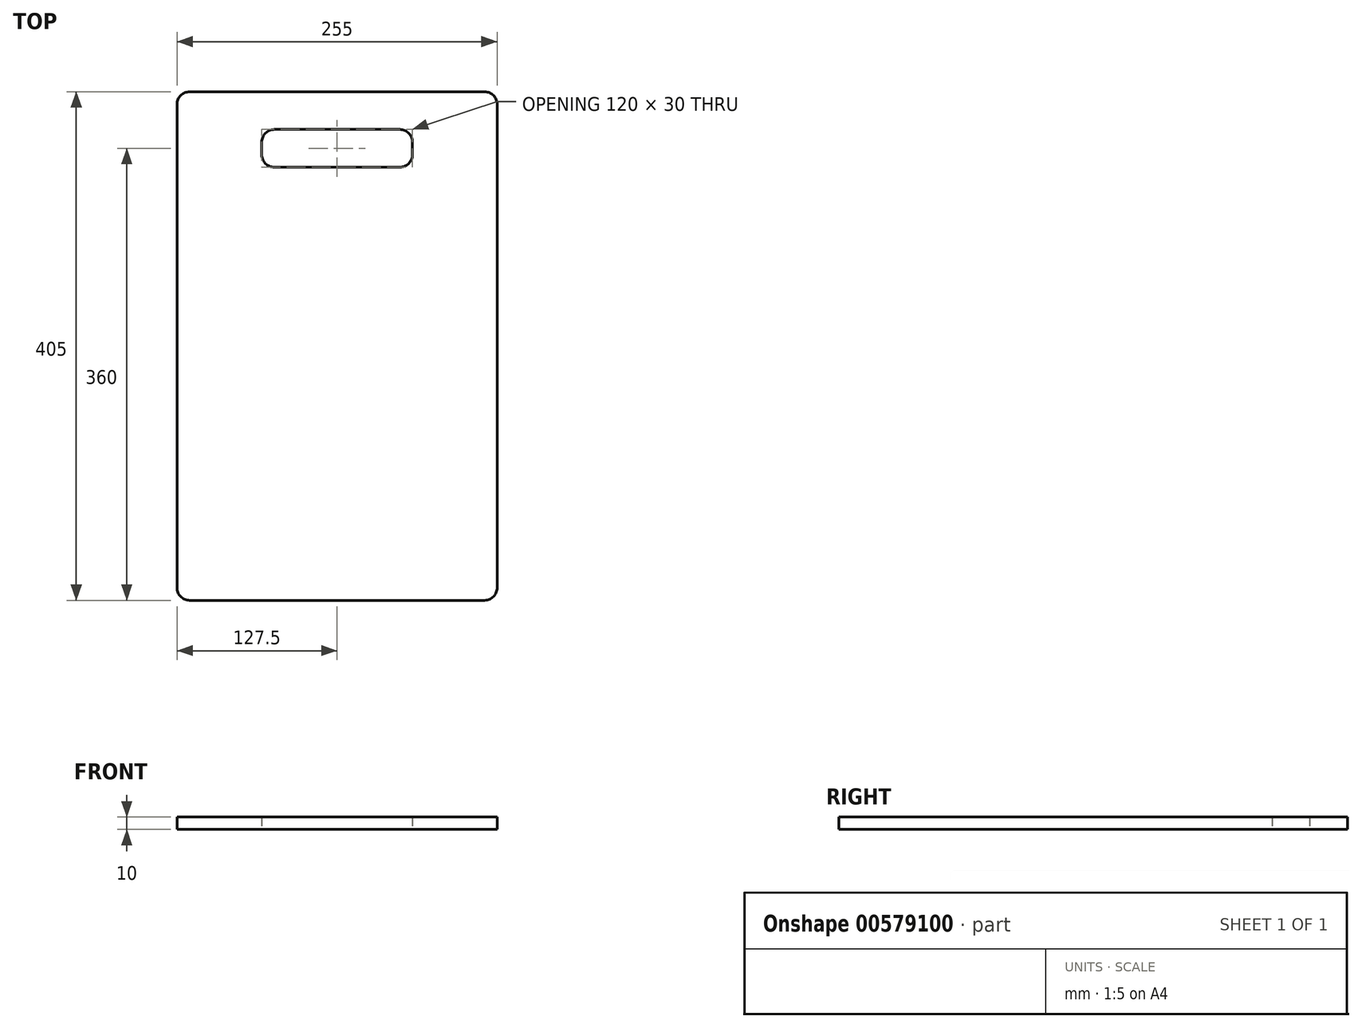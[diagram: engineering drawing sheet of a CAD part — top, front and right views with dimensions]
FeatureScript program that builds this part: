
annotation { "Feature Type Name" : "Feature", "Feature Type Description" : "" }
export const myFeature = defineFeature(function(context is Context, id is Id, definition is map)
    precondition{}
    {
        {
            var Q0;
            Q0=qCreatedBy(makeId("Top.planeOp"),FACE);
            var sketch = newSketch(context, id + "F0", { "sketchPlane" : qUnion([Q0])});
            skLineSegment(sketch, "E0.bottom", {"start": v(127.5, 202.5) * mm, "end": v(-127.5, 202.5) * mm});
            skLineSegment(sketch, "E0.top", {"start": v(127.5, -202.5) * mm, "end": v(-127.5, -202.5) * mm});
            skLineSegment(sketch, "E0.left", {"start": v(127.5, 202.5) * mm, "end": v(127.5, -202.5) * mm});
            skLineSegment(sketch, "E0.right", {"start": v(-127.5, 202.5) * mm, "end": v(-127.5, -202.5) * mm});
            skPoint(sketch, "E0.middle", {"position": v(0, 0) * mm});
            skLineSegment(sketch, "E1.bottom", {"start": v(-60, 172.5) * mm, "end": v(60, 172.5) * mm});
            skLineSegment(sketch, "E1.top", {"start": v(-60, 142.5) * mm, "end": v(60, 142.5) * mm});
            skLineSegment(sketch, "E1.left", {"start": v(-60, 172.5) * mm, "end": v(-60, 142.5) * mm});
            skLineSegment(sketch, "E1.right", {"start": v(60, 172.5) * mm, "end": v(60, 142.5) * mm});
            skLineSegment(sketch, "E2", {"start": v(0, 0) * mm, "end": v(0, 279.36) * mm, "construction": true});
            skSolve(sketch);
        }
        {
            var Q0;
            Q0=qSketchRegion(id+"F0",true);
            extrude(context, id + "F1", {"entities" : qUnion([Q0]), "depth" : 10 * mm, "offsetDistance" : 25 * mm});
        }
        {
            var Q0;
            Q0=makeQuery(id+"F1.opExtrude","SWEPT_EDGE",EDGE,{"disambiguationData":[OSD([sQuery(id+"F0.wireOp",EDGE,"E0.bottom"),sQuery(id+"F0.wireOp",EDGE,"E0.right")])]});
            var Q1;
            Q1=makeQuery(id+"F1.opExtrude","SWEPT_EDGE",EDGE,{"disambiguationData":[OSD([sQuery(id+"F0.wireOp",EDGE,"E0.bottom"),sQuery(id+"F0.wireOp",EDGE,"E0.left")])]});
            var Q2;
            Q2=makeQuery(id+"F1.opExtrude","SWEPT_EDGE",EDGE,{"disambiguationData":[OSD([sQuery(id+"F0.wireOp",EDGE,"E1.top"),sQuery(id+"F0.wireOp",EDGE,"E1.right")])]});
            var Q3;
            Q3=makeQuery(id+"F1.opExtrude","SWEPT_EDGE",EDGE,{"disambiguationData":[OSD([sQuery(id+"F0.wireOp",EDGE,"E1.bottom"),sQuery(id+"F0.wireOp",EDGE,"E1.right")])]});
            var Q4;
            Q4=makeQuery(id+"F1.opExtrude","SWEPT_EDGE",EDGE,{"disambiguationData":[OSD([sQuery(id+"F0.wireOp",EDGE,"E1.bottom"),sQuery(id+"F0.wireOp",EDGE,"E1.left")])]});
            var Q5;
            Q5=makeQuery(id+"F1.opExtrude","SWEPT_EDGE",EDGE,{"disambiguationData":[OSD([sQuery(id+"F0.wireOp",EDGE,"E1.top"),sQuery(id+"F0.wireOp",EDGE,"E1.left")])]});
            var Q6;
            Q6=makeQuery(id+"F1.opExtrude","SWEPT_EDGE",EDGE,{"disambiguationData":[OSD([sQuery(id+"F0.wireOp",EDGE,"E0.top"),sQuery(id+"F0.wireOp",EDGE,"E0.left")])]});
            var Q7;
            Q7=makeQuery(id+"F1.opExtrude","SWEPT_EDGE",EDGE,{"disambiguationData":[OSD([sQuery(id+"F0.wireOp",EDGE,"E0.top"),sQuery(id+"F0.wireOp",EDGE,"E0.right")])]});
            fillet(context, id + "F2", {"entities" : qUnion([Q0, Q1, Q2, Q3, Q4, Q5, Q6, Q7]), "radius" : 10 * mm, "tangentPropagation" : true, "allowEdgeOverflow" : false});
        }
    });
